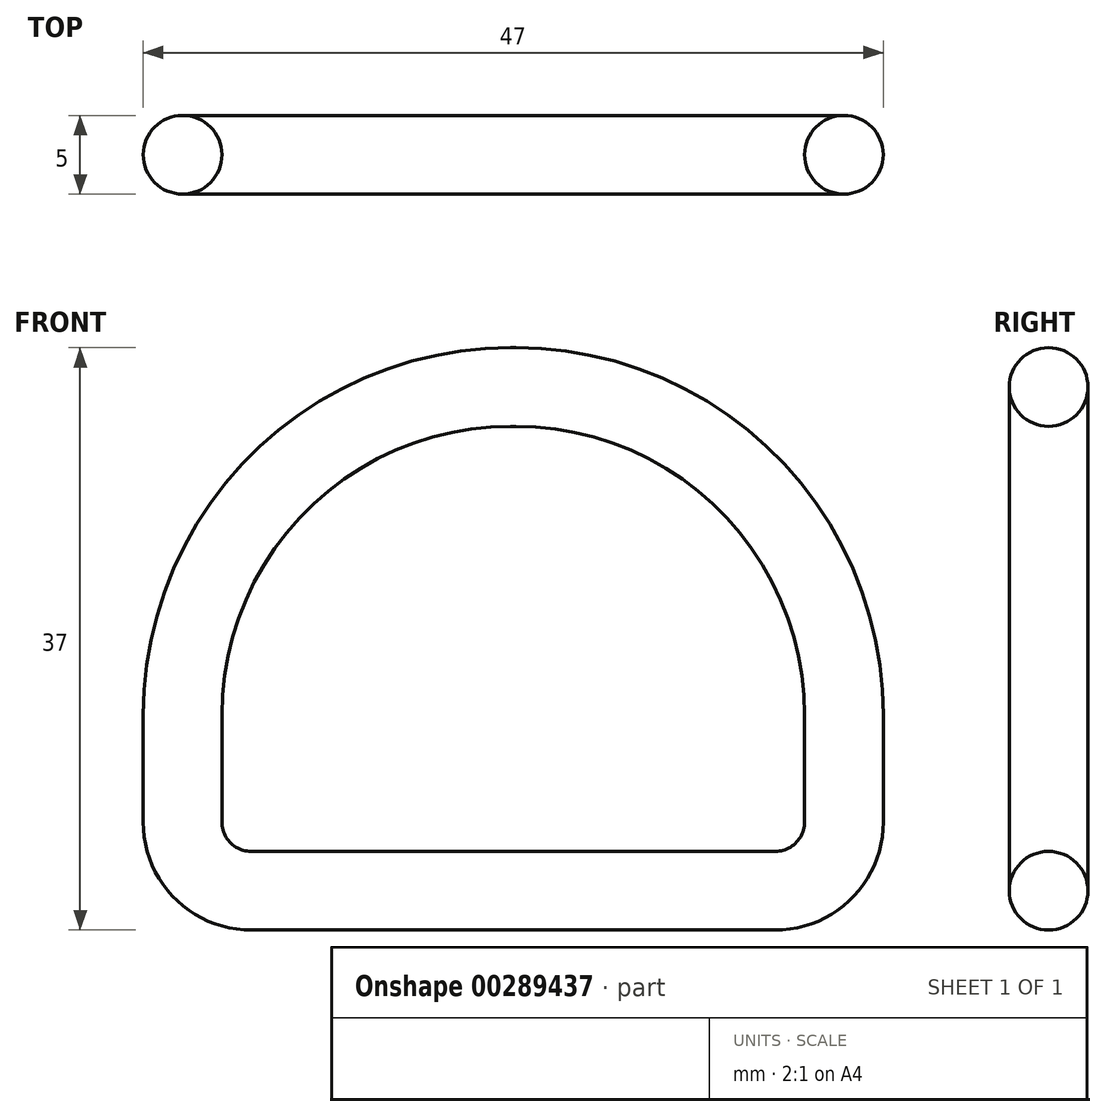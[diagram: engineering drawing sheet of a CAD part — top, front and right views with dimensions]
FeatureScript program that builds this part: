
annotation { "Feature Type Name" : "Feature", "Feature Type Description" : "" }
export const myFeature = defineFeature(function(context is Context, id is Id, definition is map)
    precondition{}
    {
        {
            var Q0;
            Q0=qCreatedBy(makeId("Front.planeOp"),FACE);
            var sketch = newSketch(context, id + "F0", { "sketchPlane" : qUnion([Q0])});
            skLineSegment(sketch, "E0.bottom", {"start": v(0.17, 18.5) * mm, "end": v(-0.17, 18.5) * mm});
            skLineSegment(sketch, "E0.top", {"start": v(16.64, -18.5) * mm, "end": v(-16.64, -18.5) * mm});
            skLineSegment(sketch, "E0.left", {"start": v(23.5, -4.83) * mm, "end": v(23.5, -11.64) * mm});
            skLineSegment(sketch, "E0.right", {"start": v(-23.5, -4.83) * mm, "end": v(-23.5, -11.64) * mm});
            skPoint(sketch, "E0.middle", {"position": v(0, 0) * mm});
            skPoint(sketch, "E1.visualSharp", {"position": v(-23.5, 18.5) * mm});
            skArc(sketch, "E1.filletArc", {"start": v(-0.17, 18.5) * mm, "mid": v(-16.67, 11.67) * mm, "end": v(-23.5, -4.83) * mm});
            skPoint(sketch, "E2.visualSharp", {"position": v(23.5, 18.5) * mm});
            skArc(sketch, "E2.filletArc", {"start": v(23.5, -4.83) * mm, "mid": v(16.67, 11.67) * mm, "end": v(0.17, 18.5) * mm});
            skPoint(sketch, "E3.visualSharp", {"position": v(-23.5, -18.5) * mm});
            skArc(sketch, "E3.filletArc", {"start": v(-23.5, -11.64) * mm, "mid": v(-21.5, -16.5) * mm, "end": v(-16.64, -18.5) * mm});
            skPoint(sketch, "E4.visualSharp", {"position": v(23.5, -18.5) * mm});
            skArc(sketch, "E4.filletArc", {"start": v(16.64, -18.5) * mm, "mid": v(21.5, -16.5) * mm, "end": v(23.5, -11.64) * mm});
            skLineSegment(sketch, "E5.0", {"start": v(0.17, 13.5) * mm, "end": v(-0.17, 13.5) * mm});
            skArc(sketch, "E5.1", {"start": v(18.5, -4.83) * mm, "mid": v(13.13, 8.13) * mm, "end": v(0.17, 13.5) * mm});
            skArc(sketch, "E5.2", {"start": v(-0.17, 13.5) * mm, "mid": v(-13.13, 8.13) * mm, "end": v(-18.5, -4.83) * mm});
            skLineSegment(sketch, "E5.3", {"start": v(18.5, -4.83) * mm, "end": v(18.5, -11.64) * mm});
            skLineSegment(sketch, "E5.4", {"start": v(-18.5, -4.83) * mm, "end": v(-18.5, -11.64) * mm});
            skArc(sketch, "E5.5", {"start": v(-18.5, -11.64) * mm, "mid": v(-17.96, -12.96) * mm, "end": v(-16.64, -13.5) * mm});
            skLineSegment(sketch, "E5.6", {"start": v(16.64, -13.5) * mm, "end": v(-16.64, -13.5) * mm});
            skArc(sketch, "E5.7", {"start": v(16.64, -13.5) * mm, "mid": v(17.96, -12.96) * mm, "end": v(18.5, -11.64) * mm});
            skSolve(sketch);
        }
        {
            var Q0;
            Q0=makeQuery(id+"F0.imprint","IMPRINT",FACE,{"disambiguationData":[TD([[makeQuery(id+"F0.imprint","IMPRINT",EDGE,{"derivedFrom":sQuery(id+"F0.wireOp",EDGE,"E0.bottom")}),1.0]])]});
            extrude(context, id + "F1", {"entities" : qUnion([Q0]), "endBound" : BoundingType.SYMMETRIC, "depth" : 5 * mm});
        }
        {
            var Q0;
            Q0=makeQuery(id+"F1.opExtrude","CAP_FACE",FACE,{"disambiguationData":[OSD([sQuery(id+"F0.wireOp",EDGE,"E0.bottom"),sQuery(id+"F0.wireOp",EDGE,"E0.top"),sQuery(id+"F0.wireOp",EDGE,"E0.left"),sQuery(id+"F0.wireOp",EDGE,"E0.right"),sQuery(id+"F0.wireOp",EDGE,"E1.filletArc"),sQuery(id+"F0.wireOp",EDGE,"E2.filletArc"),sQuery(id+"F0.wireOp",EDGE,"E3.filletArc"),sQuery(id+"F0.wireOp",EDGE,"E4.filletArc"),sQuery(id+"F0.wireOp",EDGE,"E5.0"),sQuery(id+"F0.wireOp",EDGE,"E5.1"),sQuery(id+"F0.wireOp",EDGE,"E5.2"),sQuery(id+"F0.wireOp",EDGE,"E5.3"),sQuery(id+"F0.wireOp",EDGE,"E5.4"),sQuery(id+"F0.wireOp",EDGE,"E5.5"),sQuery(id+"F0.wireOp",EDGE,"E5.6"),sQuery(id+"F0.wireOp",EDGE,"E5.7")])],"isStart":true});
            var Q1;
            Q1=makeQuery(id+"F1.opExtrude","CAP_FACE",FACE,{"disambiguationData":[OSD([sQuery(id+"F0.wireOp",EDGE,"E0.bottom"),sQuery(id+"F0.wireOp",EDGE,"E0.top"),sQuery(id+"F0.wireOp",EDGE,"E0.left"),sQuery(id+"F0.wireOp",EDGE,"E0.right"),sQuery(id+"F0.wireOp",EDGE,"E1.filletArc"),sQuery(id+"F0.wireOp",EDGE,"E2.filletArc"),sQuery(id+"F0.wireOp",EDGE,"E3.filletArc"),sQuery(id+"F0.wireOp",EDGE,"E4.filletArc"),sQuery(id+"F0.wireOp",EDGE,"E5.0"),sQuery(id+"F0.wireOp",EDGE,"E5.1"),sQuery(id+"F0.wireOp",EDGE,"E5.2"),sQuery(id+"F0.wireOp",EDGE,"E5.3"),sQuery(id+"F0.wireOp",EDGE,"E5.4"),sQuery(id+"F0.wireOp",EDGE,"E5.5"),sQuery(id+"F0.wireOp",EDGE,"E5.6"),sQuery(id+"F0.wireOp",EDGE,"E5.7")])],"isStart":false});
            fillet(context, id + "F2", {"entities" : qUnion([Q0, Q1]), "radius" : 2.5 * mm, "tangentPropagation" : true, "allowEdgeOverflow" : false});
        }
    });
